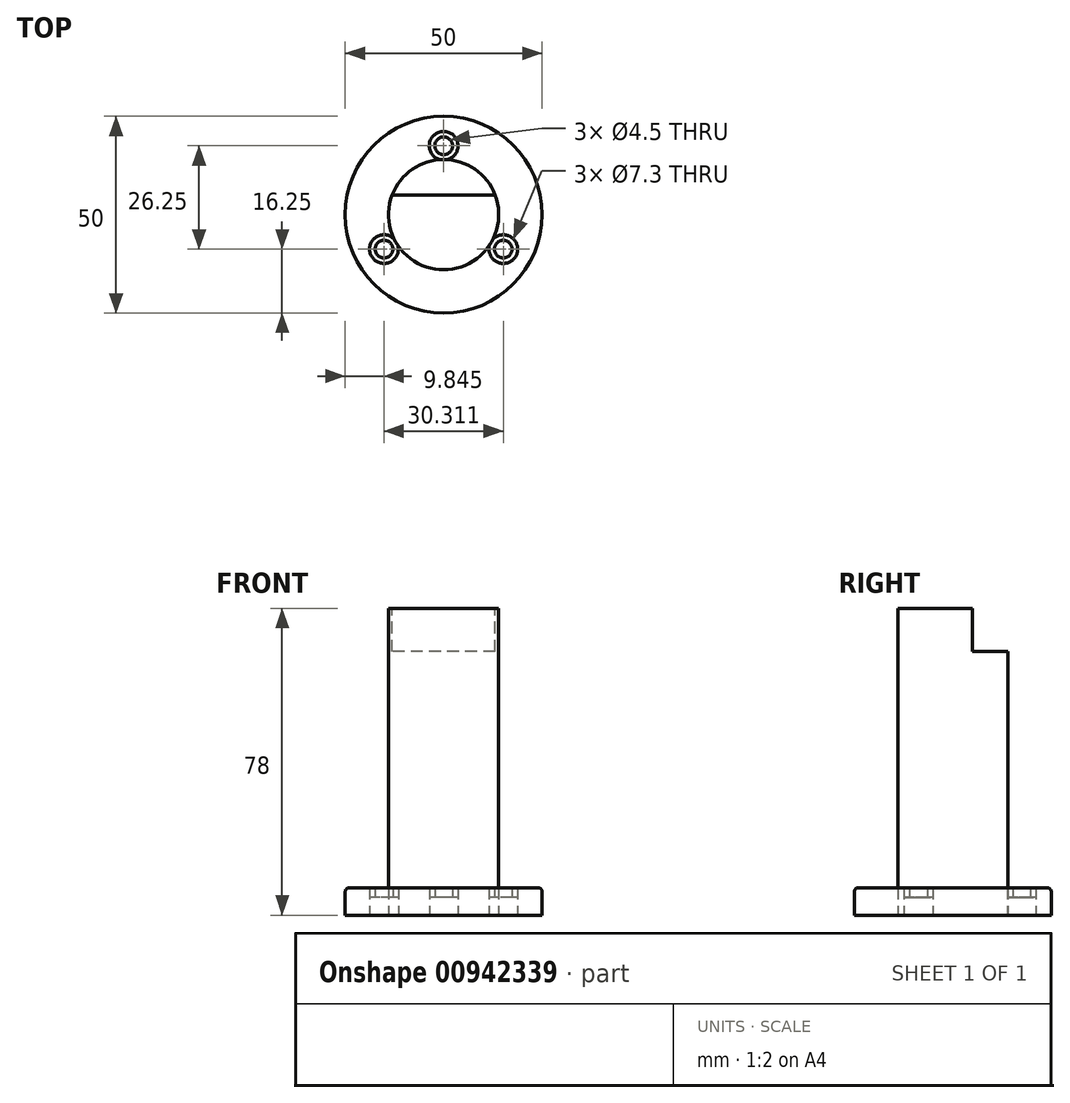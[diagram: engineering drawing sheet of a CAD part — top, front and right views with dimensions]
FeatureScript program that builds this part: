
annotation { "Feature Type Name" : "Feature", "Feature Type Description" : "" }
export const myFeature = defineFeature(function(context is Context, id is Id, definition is map)
    precondition{}
    {
        {
            var Q0;
            Q0=qCreatedBy(makeId("Top.planeOp"),FACE);
            var sketch = newSketch(context, id + "F0", { "sketchPlane" : qUnion([Q0])});
            skCircle(sketch, "E0", {"center": v(0, 0) * mm, "radius": 25 * mm});
            skCircle(sketch, "E1", {"center": v(0, 17.5) * mm, "radius": 2.25 * mm});
            skCircle(sketch, "E2.1.0", {"center": v(-15.16, -8.75) * mm, "radius": 2.25 * mm});
            skCircle(sketch, "E2.2.0", {"center": v(15.16, -8.75) * mm, "radius": 2.25 * mm});
            skCircle(sketch, "E3", {"center": v(0, 17.5) * mm, "radius": 3.65 * mm});
            skCircle(sketch, "E4", {"center": v(-15.16, -8.75) * mm, "radius": 3.65 * mm});
            skCircle(sketch, "E5", {"center": v(15.16, -8.75) * mm, "radius": 3.65 * mm});
            skSolve(sketch);
        }
        {
            var Q0;
            Q0=qCreatedBy(makeId("Top.planeOp"),FACE);
            var sketch = newSketch(context, id + "F1", { "sketchPlane" : qUnion([Q0])});
            skCircle(sketch, "E6", {"center": v(0, 0) * mm, "radius": 14 * mm});
            skSolve(sketch);
        }
        {
            var Q0;
            Q0=makeQuery(id+"F0.imprint","IMPRINT",FACE,{"disambiguationData":[TD([[makeQuery(id+"F0.imprint","IMPRINT",EDGE,{"derivedFrom":sQuery(id+"F0.wireOp",EDGE,"E0")}),1.0]])]});
            extrude(context, id + "F2", {"entities" : qUnion([Q0]), "depth" : 7 * mm, "offsetDistance" : 25 * mm});
        }
        {
            var Q0;
            Q0=makeQuery(id+"F1.imprint","IMPRINT",FACE,{"disambiguationData":[TD([[makeQuery(id+"F1.imprint","IMPRINT",EDGE,{"derivedFrom":sQuery(id+"F1.wireOp",EDGE,"E6")}),1.0]])]});
            extrude(context, id + "F3", {"entities" : qUnion([Q0]), "depth" : 78 * mm, "offsetDistance" : 25 * mm});
        }
        {
            var Q0;
            Q0=makeQuery(id+"F2.opExtrude","CAP_EDGE",EDGE,{"disambiguationData":[OSD([sQuery(id+"F0.wireOp",EDGE,"E0")])],"isStart":false});
            fillet(context, id + "F4", {"entities" : qUnion([Q0]), "radius" : 1 * mm, "tangentPropagation" : true, "allowEdgeOverflow" : false});
        }
        {
            var Q0;
            Q0=makeQuery(id+"F0.imprint","IMPRINT",FACE,{"disambiguationData":[TD([[makeQuery(id+"F0.imprint","IMPRINT",EDGE,{"derivedFrom":sQuery(id+"F0.wireOp",EDGE,"E1")}),-1.0]])]});
            var Q1;
            Q1=makeQuery(id+"F0.imprint","IMPRINT",FACE,{"disambiguationData":[TD([[makeQuery(id+"F0.imprint","IMPRINT",EDGE,{"derivedFrom":sQuery(id+"F0.wireOp",EDGE,"E2.2.0")}),-1.0]])]});
            var Q2;
            Q2=makeQuery(id+"F0.imprint","IMPRINT",FACE,{"disambiguationData":[TD([[makeQuery(id+"F0.imprint","IMPRINT",EDGE,{"derivedFrom":sQuery(id+"F0.wireOp",EDGE,"E2.1.0")}),-1.0]])]});
            extrude(context, id + "F5", {"entities" : qUnion([Q0, Q1, Q2]), "depth" : 2.5 * mm, "offsetDistance" : 25 * mm});
        }
        {
            var Q0;
            Q0=makeQuery(id+"F5.opExtrude","SWEPT_BODY",BODY,{"disambiguationData":[OSD([sQuery(id+"F0.wireOp",EDGE,"E2.1.0"),sQuery(id+"F0.wireOp",EDGE,"E4")])]});
            var Q1;
            Q1=qCreatedBy(makeId("Top.planeOp"),FACE);
            transform(context, id + "F6", {"entities" : qUnion([Q0]), "transformType" : TransformType.TRANSLATION_DISTANCE, "transformDirection" : qUnion([Q1]), "distance" : 4.5 * mm, "makeCopy" : false});
        }
        {
            var Q0;
            Q0=makeQuery(id+"F5.opExtrude","SWEPT_BODY",BODY,{"disambiguationData":[OSD([sQuery(id+"F0.wireOp",EDGE,"E1"),sQuery(id+"F0.wireOp",EDGE,"E3")])]});
            var Q1;
            Q1=makeQuery(id+"F5.opExtrude","SWEPT_BODY",BODY,{"disambiguationData":[OSD([sQuery(id+"F0.wireOp",EDGE,"E2.2.0"),sQuery(id+"F0.wireOp",EDGE,"E5")])]});
            var Q2;
            Q2=qCreatedBy(makeId("Top.planeOp"),FACE);
            transform(context, id + "F7", {"entities" : qUnion([Q0, Q1]), "transformType" : TransformType.TRANSLATION_DISTANCE, "transformDirection" : qUnion([Q2]), "distance" : 4.5 * mm, "makeCopy" : false});
        }
        {
            var Q0;
            Q0=makeQuery(id+"F3.opExtrude","CAP_FACE",FACE,{"disambiguationData":[OSD([sQuery(id+"F1.wireOp",EDGE,"E6")])],"isStart":false});
            var sketch = newSketch(context, id + "F8", { "sketchPlane" : qUnion([Q0])});
            skLineSegment(sketch, "E7.bottom", {"start": v(16.43, 5) * mm, "end": v(-16.43, 5) * mm});
            skLineSegment(sketch, "E7.top", {"start": v(16.43, 20) * mm, "end": v(-16.43, 20) * mm});
            skLineSegment(sketch, "E7.left", {"start": v(16.43, 5) * mm, "end": v(16.43, 20) * mm});
            skLineSegment(sketch, "E7.right", {"start": v(-16.43, 5) * mm, "end": v(-16.43, 20) * mm});
            skPoint(sketch, "E7.middle", {"position": v(0, 12.5) * mm});
            skSolve(sketch);
        }
        {
            var Q0;
            {var subQ0=sQuery(id+"F8.wireOp",EDGE,"E7.bottom");var subQ1=makeQuery(id+"F3.opExtrude","CAP_EDGE",EDGE,{"disambiguationData":[OSD([sQuery(id+"F1.wireOp",EDGE,"E6")])],"isStart":false});var subQ2=makeQuery(id+"F8.imprint","INTERSECT",VERTEX,{"disambiguationData":[OD(0.0)],"derivedFrom":[subQ1,subQ0]});Q0=makeQuery(id+"F8.imprint","IMPRINT",FACE,{"disambiguationData":[TD([[makeQuery(id+"F8.imprint","IMPRINT",EDGE,{"disambiguationData":[TD([[subQ2,-1.0]])],"derivedFrom":subQ0}),-1.0]])]});}
            extrude(context, id + "F9", {"entities" : qUnion([Q0]), "operationType" : NewBodyOperationType.REMOVE, "oppositeDirection" : true, "depth" : 11 * mm, "offsetDistance" : 25 * mm});
        }
    });
